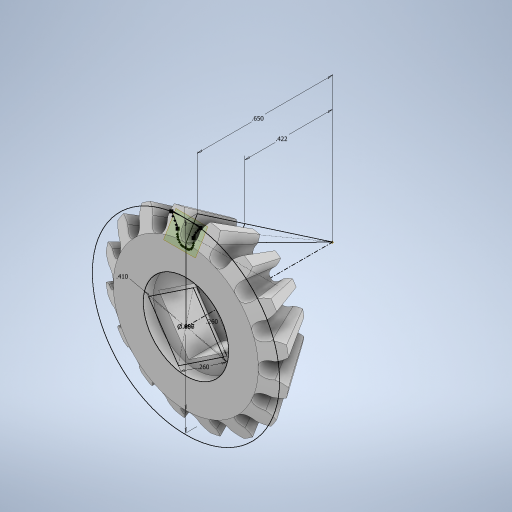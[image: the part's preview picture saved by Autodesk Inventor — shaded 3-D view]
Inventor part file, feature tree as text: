
AUTODESK INVENTOR PART (.ipt)
format: ipt  version: 2023 (Build 270158000, 158)  size: 2,094,592 bytes
history: native  units: in
note: dims shown in document units (in); Inventor stores cm internally (conversion verified against a paired STEP export)
features: extrude x6, sketch x5, move_body x3, other x2, projected_geometry x2, plane x1, revolve x1, loft x1, boolean_combine x1, pattern_circular x1, chamfer x1
ambient origin geometry x8: Origin, YZ Plane, XZ Plane, XY Plane, X Axis, Y Axis, Z Axis, Center Point
bodies: Solid3 (feature_tree), Solid4 (feature_tree)
feature tree (24):
  extrude  "Extrusion2"  [1 undecoded]
  plane  "Work Plane1"
  move_body  "Move Body1"
  revolve  "Revolution1"  [1 undecoded]
  move_body  "Move Body2"
  move_body  "Move Body3"
  sketch  "Sketch3"  dims[d8=0.697in d9=0.65in]
  other  "Work Point1"
  loft  "Loft1"
  boolean_combine  "Combine1"
  extrude  "Extrusion3"  Depth=0.004in TaperAngle=0.0deg
  pattern_circular  "Circular Pattern1"  [2 undecoded]
  sketch  "Sketch4"  dims[d11=0.422in d14=360.0deg]
  extrude  "Extrusion4"  TaperAngle=0.0deg  [1 undecoded]
  extrude  "Extrusion5"  Depth=0.0586in TaperAngle=0.0deg
  extrude  "Extrusion6"  Depth=6.2992in TaperAngle=360.0deg
  extrude  "Extrusion7"  Depth=0.26in
  chamfer  "Chamfer1"  Distance=0.26in
  sketch  "Sketch2"  dims[d3=0.0039in d4=0.0in d5=-0.2106in]
  projected_geometry  "Projected Loop1"
  other  "Edges1"
  sketch  "Sketch5"  dims[d15=0.2106in d16=0.0in d17=0.004in d18=0.0in]
  sketch  "Sketch6"  dims[d19=0.0in d20=0.0in d21=-0.062in d22=0.886in d23=0.0in d24=90.0deg d25=0.0in d26=90.0deg d27=0.0586in d28=0.0in d29=6.2992in d30=360.0deg d32=0.26in d33=0.26in d34=0.41in d35=0.05in d36=0.0in d37=0.2in d38=0.0in d39=0.13in d40=0.13in d41=0.0in d42=0.0in d43=0.25in d44=0.05in d45=0.0in d46=0.0236in d47=0.125in d48=45.0deg]
  projected_geometry  "Projected Loop2"
note: 5 required parameter values undecoded (feature->parameter linkage not recoverable at this tier; creation-order binding heuristic only, values carry confidence <= 0.55)